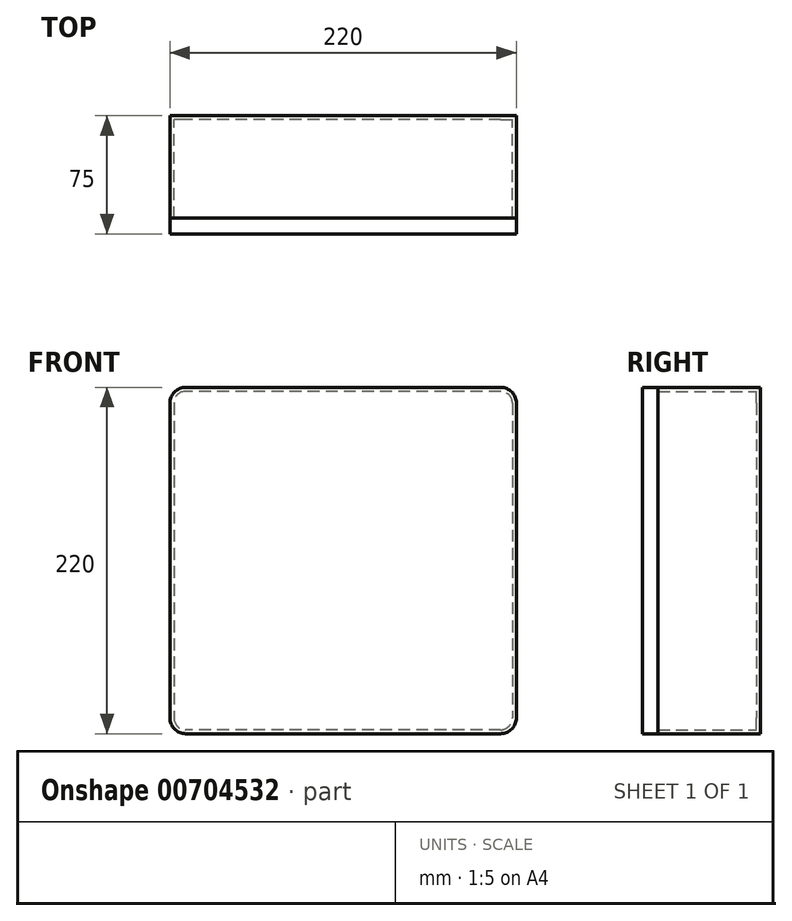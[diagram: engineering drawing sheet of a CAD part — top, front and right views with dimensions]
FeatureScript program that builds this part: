
annotation { "Feature Type Name" : "Feature", "Feature Type Description" : "" }
export const myFeature = defineFeature(function(context is Context, id is Id, definition is map)
    precondition{}
    {
        {
            var Q0;
            Q0=qCreatedBy(makeId("Front.planeOp"),FACE);
            var sketch = newSketch(context, id + "F0", { "sketchPlane" : qUnion([Q0])});
            skLineSegment(sketch, "E0.bottom", {"start": v(110, 110) * mm, "end": v(-110, 110) * mm});
            skLineSegment(sketch, "E0.top", {"start": v(110, -110) * mm, "end": v(-110, -110) * mm});
            skLineSegment(sketch, "E0.left", {"start": v(110, 110) * mm, "end": v(110, -110) * mm});
            skLineSegment(sketch, "E0.right", {"start": v(-110, 110) * mm, "end": v(-110, -110) * mm});
            skPoint(sketch, "E0.middle", {"position": v(0, 0) * mm});
            skSolve(sketch);
        }
        {
            var Q0;
            Q0=makeQuery(id+"F0.imprint","IMPRINT",FACE,{"disambiguationData":[TD([[makeQuery(id+"F0.imprint","IMPRINT",EDGE,{"derivedFrom":sQuery(id+"F0.wireOp",EDGE,"E0.bottom")}),1.0]])]});
            extrude(context, id + "F1", {"entities" : qUnion([Q0]), "depth" : 65 * mm, "offsetDistance" : 25 * mm});
        }
        {
            var Q0;
            Q0=makeQuery(id+"F1.opExtrude","SWEPT_EDGE",EDGE,{"disambiguationData":[OSD([sQuery(id+"F0.wireOp",EDGE,"E0.bottom"),sQuery(id+"F0.wireOp",EDGE,"E0.left")])]});
            var Q1;
            Q1=makeQuery(id+"F1.opExtrude","SWEPT_EDGE",EDGE,{"disambiguationData":[OSD([sQuery(id+"F0.wireOp",EDGE,"E0.bottom"),sQuery(id+"F0.wireOp",EDGE,"E0.right")])]});
            var Q2;
            Q2=makeQuery(id+"F1.opExtrude","SWEPT_EDGE",EDGE,{"disambiguationData":[OSD([sQuery(id+"F0.wireOp",EDGE,"E0.top"),sQuery(id+"F0.wireOp",EDGE,"E0.left")])]});
            var Q3;
            Q3=makeQuery(id+"F1.opExtrude","SWEPT_EDGE",EDGE,{"disambiguationData":[OSD([sQuery(id+"F0.wireOp",EDGE,"E0.top"),sQuery(id+"F0.wireOp",EDGE,"E0.right")])]});
            fillet(context, id + "F2", {"entities" : qUnion([Q0, Q1, Q2, Q3]), "radius" : 10 * mm, "tangentPropagation" : true, "allowEdgeOverflow" : false});
        }
        {
            var Q0;
            Q0=makeQuery(id+"F1.opExtrude","CAP_FACE",FACE,{"disambiguationData":[OSD([sQuery(id+"F0.wireOp",EDGE,"E0.bottom"),sQuery(id+"F0.wireOp",EDGE,"E0.top"),sQuery(id+"F0.wireOp",EDGE,"E0.left"),sQuery(id+"F0.wireOp",EDGE,"E0.right")])],"isStart":false});
            shell(context, id + "F3", {"entities" : qUnion([Q0]), "thickness" : 2.5 * mm});
        }
        {
            var Q0;
            Q0=makeQuery(id+"F1.opExtrude","CAP_FACE",FACE,{"disambiguationData":[OSD([sQuery(id+"F0.wireOp",EDGE,"E0.bottom"),sQuery(id+"F0.wireOp",EDGE,"E0.top"),sQuery(id+"F0.wireOp",EDGE,"E0.left"),sQuery(id+"F0.wireOp",EDGE,"E0.right")])],"isStart":false});
            var sketch = newSketch(context, id + "F4", { "sketchPlane" : qUnion([Q0])});
            skLineSegment(sketch, "E1.bottom", {"start": v(100, 110) * mm, "end": v(-100, 110) * mm});
            skLineSegment(sketch, "E1.top", {"start": v(100, -110) * mm, "end": v(-100, -110) * mm});
            skLineSegment(sketch, "E1.left", {"start": v(110, 100) * mm, "end": v(110, -100) * mm});
            skLineSegment(sketch, "E1.right", {"start": v(-110, 100) * mm, "end": v(-110, -100) * mm});
            skPoint(sketch, "E1.middle", {"position": v(0, 0) * mm});
            skPoint(sketch, "E2.visualSharp", {"position": v(-110, 110) * mm});
            skArc(sketch, "E2.filletArc", {"start": v(-100, 110) * mm, "mid": v(-107.07, 107.07) * mm, "end": v(-110, 100) * mm});
            skPoint(sketch, "E3.visualSharp", {"position": v(110, 110) * mm});
            skArc(sketch, "E3.filletArc", {"start": v(110, 100) * mm, "mid": v(107.07, 107.07) * mm, "end": v(100, 110) * mm});
            skPoint(sketch, "E4.visualSharp", {"position": v(110, -110) * mm});
            skArc(sketch, "E4.filletArc", {"start": v(100, -110) * mm, "mid": v(107.07, -107.07) * mm, "end": v(110, -100) * mm});
            skPoint(sketch, "E5.visualSharp", {"position": v(-110, -110) * mm});
            skArc(sketch, "E5.filletArc", {"start": v(-110, -100) * mm, "mid": v(-107.07, -107.07) * mm, "end": v(-100, -110) * mm});
            skSolve(sketch);
        }
        {
            var Q0;
            Q0 = qSketchRegion(id + "F4", true);
            extrude(context, id + "F5", {"entities" : qUnion([Q0]), "depth" : 10 * mm, "offsetDistance" : 25 * mm});
        }
    });
